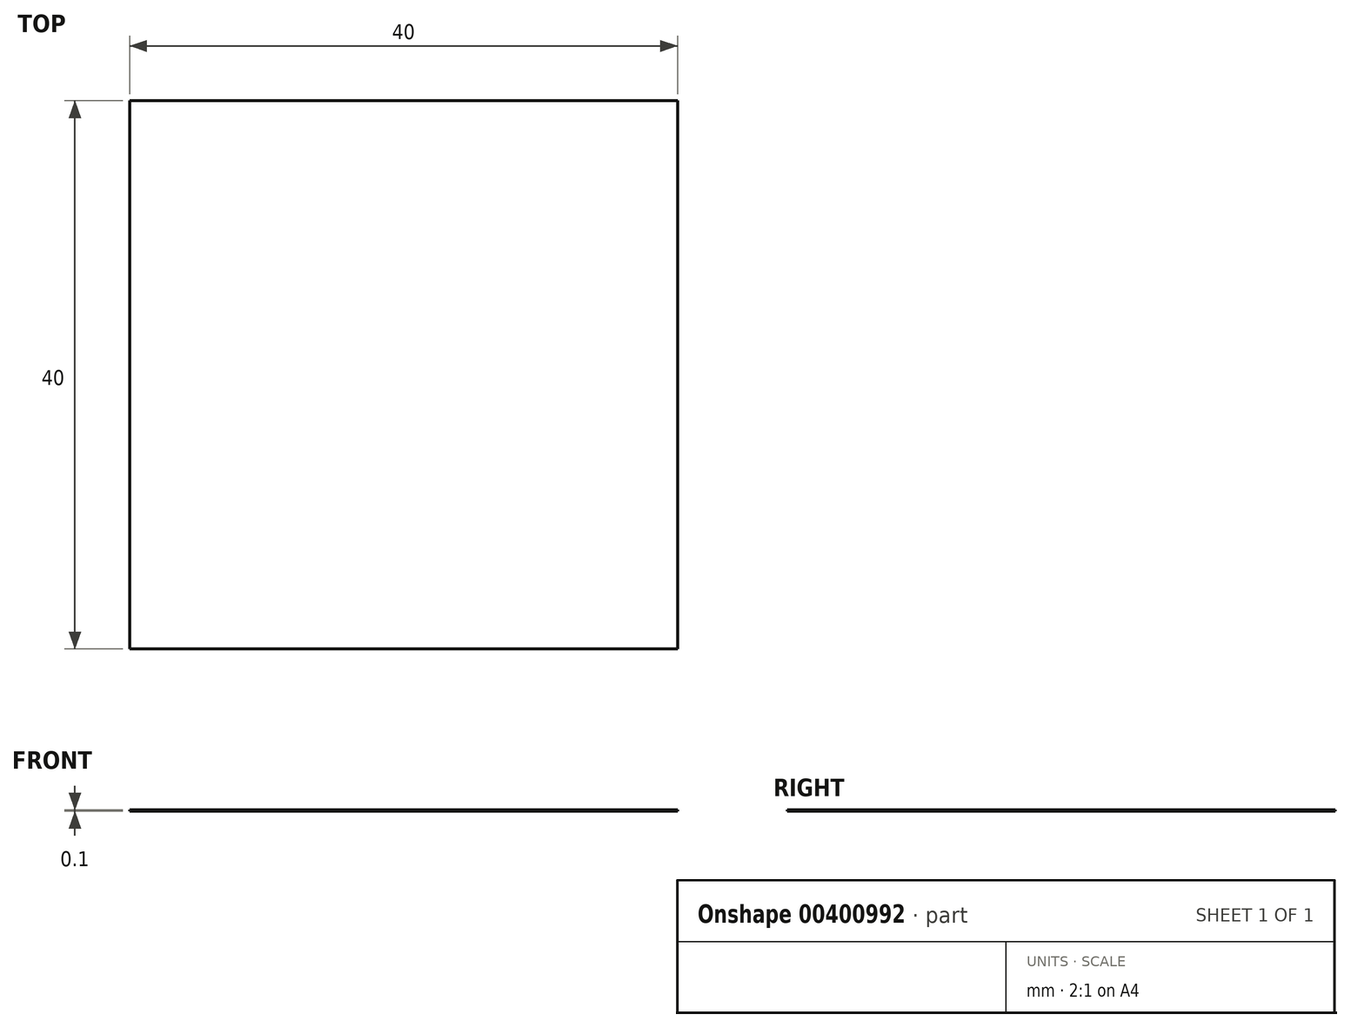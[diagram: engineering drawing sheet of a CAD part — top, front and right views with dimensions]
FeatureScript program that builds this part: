
annotation { "Feature Type Name" : "Feature", "Feature Type Description" : "" }
export const myFeature = defineFeature(function(context is Context, id is Id, definition is map)
    precondition{}
    {
        {
            var Q0;
            Q0=qCreatedBy(makeId("Top.planeOp"),FACE);
            var sketch = newSketch(context, id + "F0", { "sketchPlane" : qUnion([Q0])});
            skLineSegment(sketch, "E0.bottom", {"start": v(20, -20) * mm, "end": v(-20, -20) * mm});
            skLineSegment(sketch, "E0.top", {"start": v(20, 20) * mm, "end": v(-20, 20) * mm});
            skLineSegment(sketch, "E0.left", {"start": v(20, -20) * mm, "end": v(20, 20) * mm});
            skLineSegment(sketch, "E0.right", {"start": v(-20, -20) * mm, "end": v(-20, 20) * mm});
            skPoint(sketch, "E0.middle", {"position": v(0, 0) * mm});
            skSolve(sketch);
        }
        {
            var Q0;
            Q0=makeQuery(id+"F0.imprint","IMPRINT",FACE,{"disambiguationData":[TD([[makeQuery(id+"F0.imprint","IMPRINT",EDGE,{"derivedFrom":sQuery(id+"F0.wireOp",EDGE,"E0.bottom")}),-1.0]])]});
            extrude(context, id + "F1", {"entities" : qUnion([Q0]), "depth" : 0.1 * mm});
        }
    });
